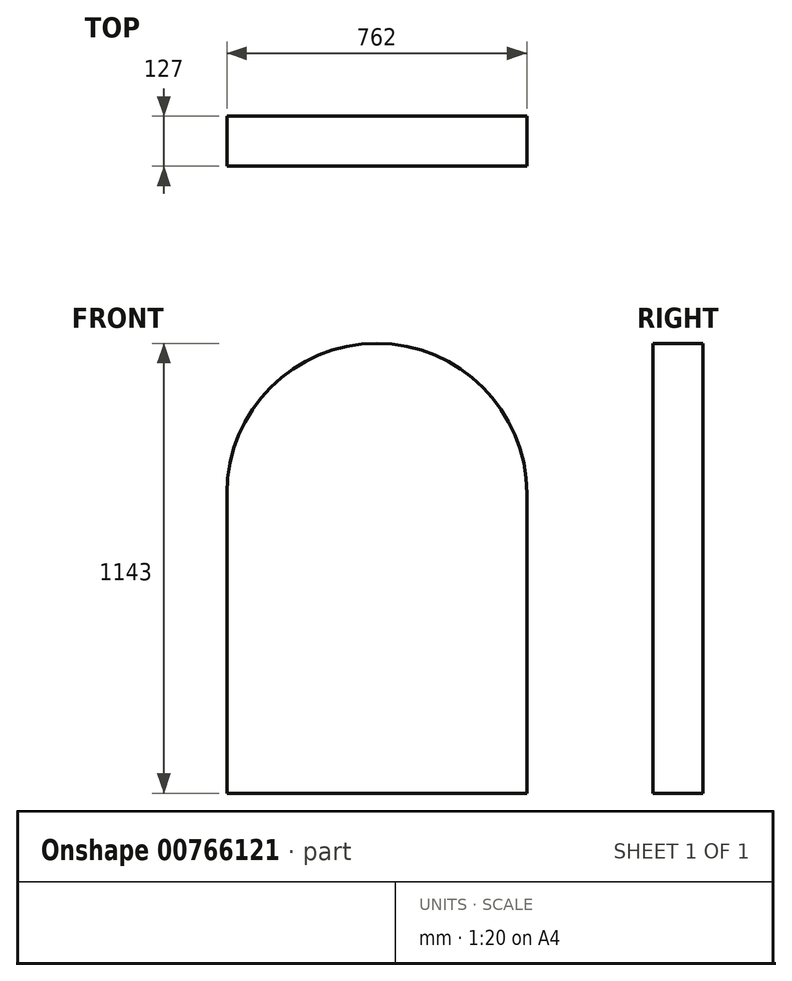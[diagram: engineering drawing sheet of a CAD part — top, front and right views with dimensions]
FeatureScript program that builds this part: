
annotation { "Feature Type Name" : "Feature", "Feature Type Description" : "" }
export const myFeature = defineFeature(function(context is Context, id is Id, definition is map)
    precondition{}
    {
        {
            var Q0;
            Q0=qCreatedBy(makeId("Front.planeOp"),FACE);
            var sketch = newSketch(context, id + "F0", { "sketchPlane" : qUnion([Q0])});
            skArc(sketch, "E0", {"start": v(461.5, 0) * mm, "mid": v(80.5, 381) * mm, "end": v(-300.5, 0) * mm});
            skLineSegment(sketch, "E1", {"start": v(-300.5, 0) * mm, "end": v(-300.5, -762) * mm});
            skLineSegment(sketch, "E2", {"start": v(461.5, 0) * mm, "end": v(461.5, -762) * mm});
            skLineSegment(sketch, "E3", {"start": v(461.5, -762) * mm, "end": v(-300.5, -762) * mm});
            skSolve(sketch);
        }
        {
            var Q0;
            Q0=makeQuery(id+"F0.imprint","IMPRINT",FACE,{"disambiguationData":[TD([[makeQuery(id+"F0.imprint","IMPRINT",EDGE,{"derivedFrom":sQuery(id+"F0.wireOp",EDGE,"E0")}),1.0]])]});
            extrude(context, id + "F1", {"entities" : qUnion([Q0]), "endBound" : BoundingType.SYMMETRIC, "depth" : 127 * mm, "offsetDistance" : 25.4 * mm});
        }
    });
